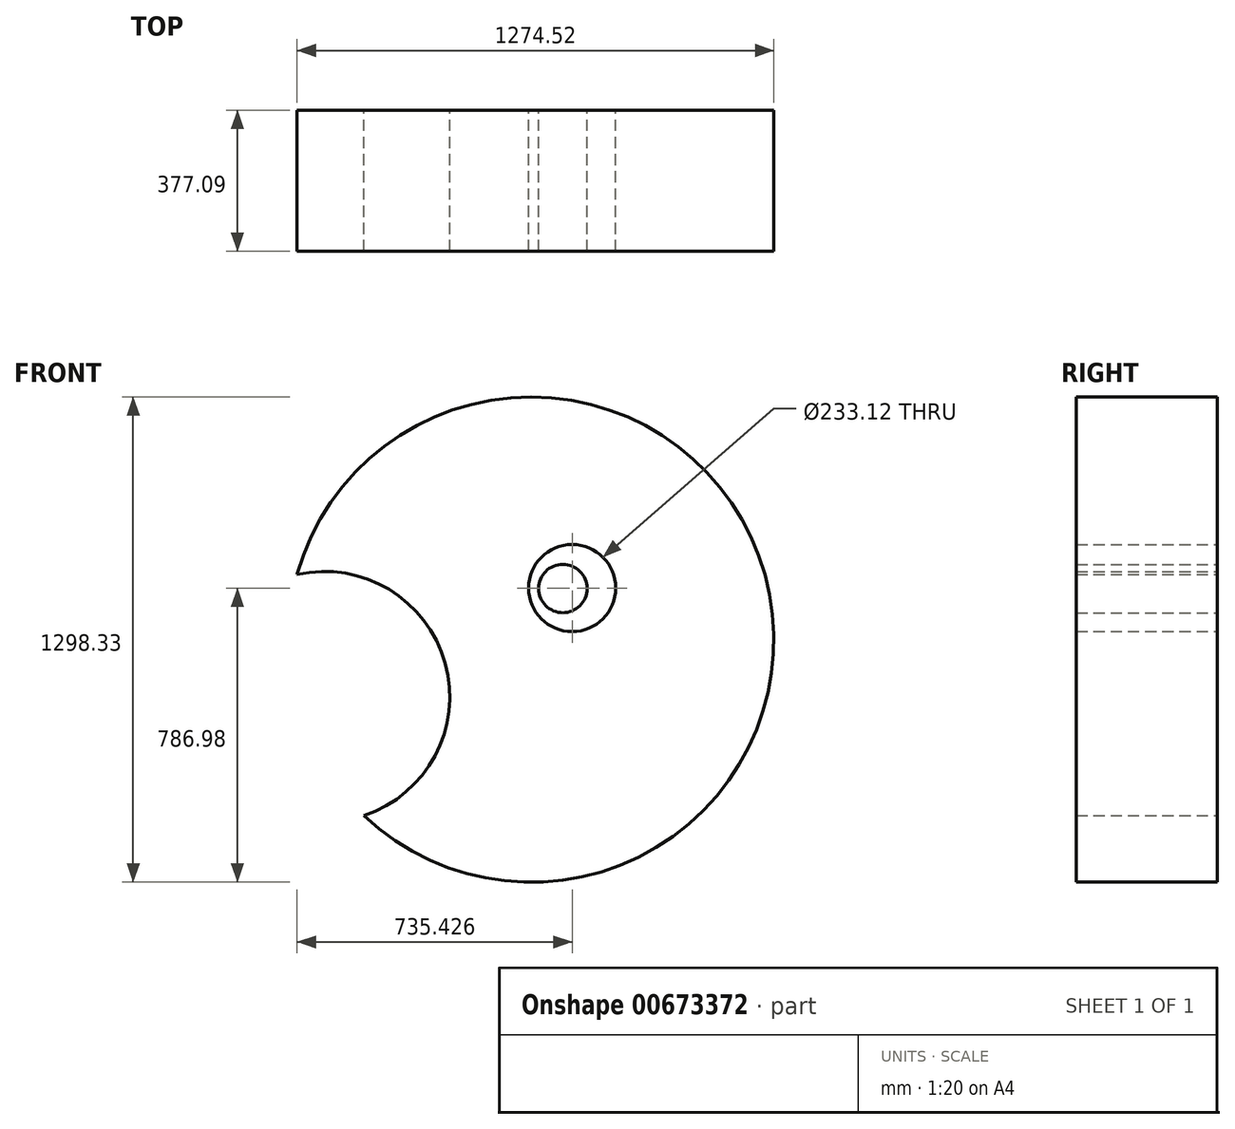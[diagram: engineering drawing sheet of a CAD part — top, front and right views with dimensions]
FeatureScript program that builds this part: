
annotation { "Feature Type Name" : "Feature", "Feature Type Description" : "" }
export const myFeature = defineFeature(function(context is Context, id is Id, definition is map)
    precondition{}
    {
        {
            var Q0;
            Q0=qCreatedBy(makeId("Front.planeOp"),FACE);
            var sketch = newSketch(context, id + "F0", { "sketchPlane" : qUnion([Q0])});
            skCircle(sketch, "E0", {"center": v(-100.78, -108.12) * mm, "radius": 116.56 * mm});
            skCircle(sketch, "E1", {"center": v(-125.72, -109.36) * mm, "radius": 64.73 * mm});
            skCircle(sketch, "E2", {"center": v(-210.85, -245.94) * mm, "radius": 649.16 * mm});
            skCircle(sketch, "E3", {"center": v(-763.47, -398.94) * mm, "radius": 335.16 * mm});
            skSolve(sketch);
        }
        {
            var Q0;
            Q0=makeQuery(id+"F0.imprint","IMPRINT",FACE,{"disambiguationData":[TD([[makeQuery(id+"F0.imprint","IMPRINT",EDGE,{"derivedFrom":sQuery(id+"F0.wireOp",EDGE,"E1")}),1.0]])]});
            var Q1;
            Q1=makeQuery(id+"F0.imprint","IMPRINT",FACE,{"disambiguationData":[TD([[makeQuery(id+"F0.imprint","IMPRINT",EDGE,{"derivedFrom":sQuery(id+"F0.wireOp",EDGE,"E0")}),-1.0]])]});
            extrude(context, id + "F1", {"entities" : qUnion([Q0, Q1]), "depth" : 377.09 * mm, "offsetDistance" : 25.4 * mm});
        }
    });
